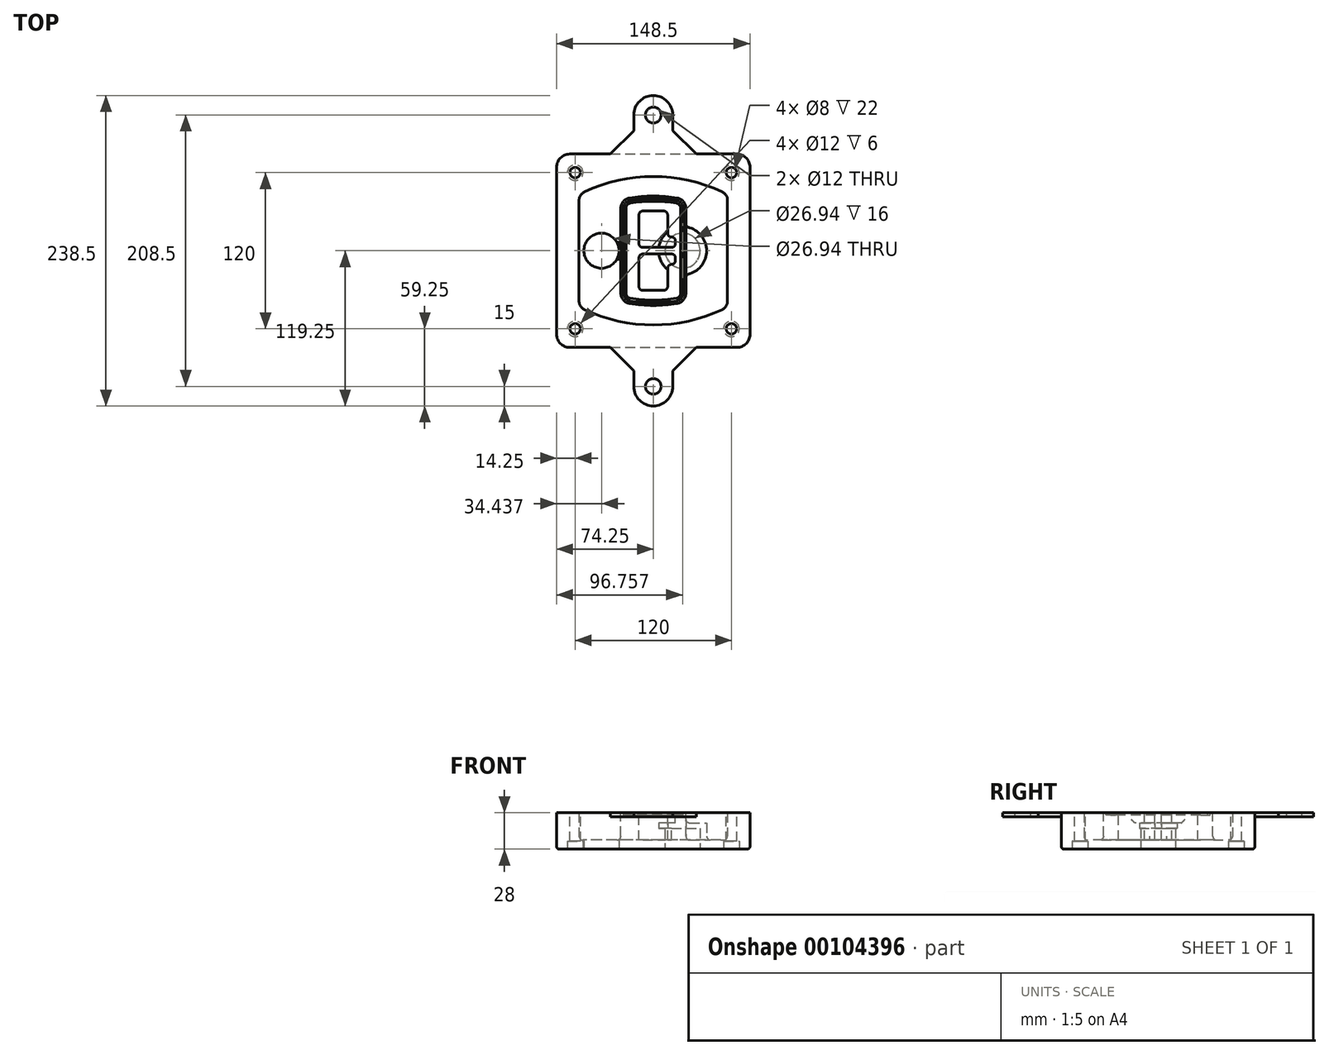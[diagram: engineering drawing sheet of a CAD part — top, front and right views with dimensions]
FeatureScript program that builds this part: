
annotation { "Feature Type Name" : "Feature", "Feature Type Description" : "" }
export const myFeature = defineFeature(function(context is Context, id is Id, definition is map)
    precondition{}
    {
        {
            var Q0;
            Q0=qCreatedBy(makeId("Top.planeOp"),FACE);
            var sketch = newSketch(context, id + "F0", { "sketchPlane" : qUnion([Q0])});
            skPoint(sketch, "E0.rect.middle", {"position": v(0, 0) * mm});
            skLineSegment(sketch, "E1.bottom", {"start": v(-64.25, -74.25) * mm, "end": v(64.25, -74.25) * mm});
            skLineSegment(sketch, "E1.top", {"start": v(-64.25, 74.25) * mm, "end": v(64.25, 74.25) * mm});
            skLineSegment(sketch, "E1.left", {"start": v(-74.25, -64.25) * mm, "end": v(-74.25, 64.25) * mm});
            skLineSegment(sketch, "E1.right", {"start": v(74.25, -64.25) * mm, "end": v(74.25, 64.25) * mm});
            skLineSegment(sketch, "E2", {"start": v(-74.25, 74.25) * mm, "end": v(74.25, -74.25) * mm, "construction": true});
            skLineSegment(sketch, "E3", {"start": v(74.25, 74.25) * mm, "end": v(-74.25, -74.25) * mm, "construction": true});
            skCircle(sketch, "E4", {"center": v(-60, 60) * mm, "radius": 4 * mm});
            skCircle(sketch, "E5", {"center": v(60, 60) * mm, "radius": 4 * mm});
            skCircle(sketch, "E6", {"center": v(60, -60) * mm, "radius": 4 * mm});
            skCircle(sketch, "E7", {"center": v(-60, -60) * mm, "radius": 4 * mm});
            skLineSegment(sketch, "E8", {"start": v(-60, 60) * mm, "end": v(60, 60) * mm, "construction": true});
            skLineSegment(sketch, "E9", {"start": v(60, 60) * mm, "end": v(60, -60) * mm, "construction": true});
            skLineSegment(sketch, "E10", {"start": v(60, -60) * mm, "end": v(-60, -60) * mm, "construction": true});
            skLineSegment(sketch, "E11", {"start": v(-60, -60) * mm, "end": v(-60, 60) * mm, "construction": true});
            skLineSegment(sketch, "E12", {"start": v(-60, 38.83) * mm, "end": v(-60, -38.83) * mm});
            skLineSegment(sketch, "E13", {"start": v(60, 38.83) * mm, "end": v(60, -38.83) * mm});
            skArc(sketch, "E14", {"start": v(54.26, 47.88) * mm, "mid": v(0, 60) * mm, "end": v(-54.26, 47.88) * mm});
            skArc(sketch, "E15", {"start": v(-54.26, -47.88) * mm, "mid": v(0, -60) * mm, "end": v(54.26, -47.88) * mm});
            skLineSegment(sketch, "E16", {"start": v(-60, 0) * mm, "end": v(60, 0) * mm, "construction": true});
            skPoint(sketch, "E17.visualSharp", {"position": v(-60, -45) * mm});
            skArc(sketch, "E17.filletArc", {"start": v(-60, -38.83) * mm, "mid": v(-58.44, -44.2) * mm, "end": v(-54.26, -47.88) * mm});
            skPoint(sketch, "E18.visualSharp", {"position": v(-60, 45) * mm});
            skArc(sketch, "E18.filletArc", {"start": v(-54.26, 47.88) * mm, "mid": v(-58.44, 44.2) * mm, "end": v(-60, 38.83) * mm});
            skPoint(sketch, "E19.visualSharp", {"position": v(60, 45) * mm});
            skArc(sketch, "E19.filletArc", {"start": v(60, 38.83) * mm, "mid": v(58.44, 44.2) * mm, "end": v(54.26, 47.88) * mm});
            skPoint(sketch, "E20.visualSharp", {"position": v(60, -45) * mm});
            skArc(sketch, "E20.filletArc", {"start": v(54.26, -47.88) * mm, "mid": v(58.44, -44.2) * mm, "end": v(60, -38.83) * mm});
            skPoint(sketch, "E21.visualSharp", {"position": v(-74.25, 74.25) * mm});
            skArc(sketch, "E21.filletArc", {"start": v(-64.25, 74.25) * mm, "mid": v(-71.32, 71.32) * mm, "end": v(-74.25, 64.25) * mm});
            skPoint(sketch, "E22.visualSharp", {"position": v(74.25, 74.25) * mm});
            skArc(sketch, "E22.filletArc", {"start": v(74.25, 64.25) * mm, "mid": v(71.32, 71.32) * mm, "end": v(64.25, 74.25) * mm});
            skPoint(sketch, "E23.visualSharp", {"position": v(74.25, -74.25) * mm});
            skArc(sketch, "E23.filletArc", {"start": v(64.25, -74.25) * mm, "mid": v(71.32, -71.32) * mm, "end": v(74.25, -64.25) * mm});
            skPoint(sketch, "E24.visualSharp", {"position": v(-74.25, -74.25) * mm});
            skArc(sketch, "E24.filletArc", {"start": v(-74.25, -64.25) * mm, "mid": v(-71.32, -71.32) * mm, "end": v(-64.25, -74.25) * mm});
            skArc(sketch, "E25.0", {"start": v(57, 38.83) * mm, "mid": v(55.9, 42.58) * mm, "end": v(52.98, 45.17) * mm});
            skLineSegment(sketch, "E25.1", {"start": v(57, 38.83) * mm, "end": v(57, -38.83) * mm});
            skArc(sketch, "E25.2", {"start": v(52.98, -45.17) * mm, "mid": v(55.9, -42.58) * mm, "end": v(57, -38.83) * mm});
            skArc(sketch, "E25.3", {"start": v(-52.98, -45.17) * mm, "mid": v(0, -57) * mm, "end": v(52.98, -45.17) * mm});
            skArc(sketch, "E25.4", {"start": v(-57, -38.83) * mm, "mid": v(-55.9, -42.58) * mm, "end": v(-52.98, -45.17) * mm});
            skArc(sketch, "E25.5", {"start": v(52.98, 45.17) * mm, "mid": v(0, 57) * mm, "end": v(-52.98, 45.17) * mm});
            skLineSegment(sketch, "E25.6", {"start": v(-57, 38.83) * mm, "end": v(-57, -38.83) * mm});
            skArc(sketch, "E25.7", {"start": v(-52.98, 45.17) * mm, "mid": v(-55.9, 42.58) * mm, "end": v(-57, 38.83) * mm});
            skArc(sketch, "E26.0", {"start": v(-55.96, 51.5) * mm, "mid": v(-61.82, 46.33) * mm, "end": v(-64, 38.83) * mm});
            skArc(sketch, "E26.1", {"start": v(55.96, 51.5) * mm, "mid": v(0, 64) * mm, "end": v(-55.96, 51.5) * mm});
            skArc(sketch, "E26.2", {"start": v(64, 38.83) * mm, "mid": v(61.82, 46.33) * mm, "end": v(55.96, 51.5) * mm});
            skLineSegment(sketch, "E26.3", {"start": v(64, 38.83) * mm, "end": v(64, -38.83) * mm});
            skArc(sketch, "E26.4", {"start": v(55.96, -51.5) * mm, "mid": v(61.82, -46.33) * mm, "end": v(64, -38.83) * mm});
            skLineSegment(sketch, "E26.5", {"start": v(-64, 38.83) * mm, "end": v(-64, -38.83) * mm});
            skArc(sketch, "E26.6", {"start": v(-55.96, -51.5) * mm, "mid": v(0, -64) * mm, "end": v(55.96, -51.5) * mm});
            skArc(sketch, "E26.7", {"start": v(-64, -38.83) * mm, "mid": v(-61.82, -46.33) * mm, "end": v(-55.96, -51.5) * mm});
            skSolve(sketch);
        }
        {
            var Q0;
            Q0=makeQuery(id+"F0.imprint","IMPRINT",FACE,{"disambiguationData":[TD([[makeQuery(id+"F0.imprint","IMPRINT",EDGE,{"derivedFrom":sQuery(id+"F0.wireOp",EDGE,"E1.bottom")}),1.0]])]});
            var Q1;
            Q1=makeQuery(id+"F0.imprint","IMPRINT",FACE,{"disambiguationData":[TD([[makeQuery(id+"F0.imprint","IMPRINT",EDGE,{"derivedFrom":sQuery(id+"F0.wireOp",EDGE,"E12")}),1.0]])]});
            var Q2;
            Q2=makeQuery(id+"F0.imprint","IMPRINT",FACE,{"disambiguationData":[TD([[makeQuery(id+"F0.imprint","IMPRINT",EDGE,{"derivedFrom":sQuery(id+"F0.wireOp",EDGE,"E25.0")}),1.0]])]});
            var Q3;
            Q3=makeQuery(id+"F0.imprint","IMPRINT",FACE,{"disambiguationData":[TD([[makeQuery(id+"F0.imprint","IMPRINT",EDGE,{"derivedFrom":sQuery(id+"F0.wireOp",EDGE,"E12")}),-1.0]])]});
            extrude(context, id + "F1", {"entities" : qUnion([Q0, Q1, Q2, Q3]), "oppositeDirection" : true, "depth" : 25 * mm});
        }
        {
            var Q0;
            Q0=makeQuery(id+"F0.imprint","IMPRINT",FACE,{"disambiguationData":[TD([[makeQuery(id+"F0.imprint","IMPRINT",EDGE,{"derivedFrom":sQuery(id+"F0.wireOp",EDGE,"E12")}),1.0]])]});
            extrude(context, id + "F2", {"entities" : qUnion([Q0]), "operationType" : NewBodyOperationType.ADD, "depth" : 3 * mm});
        }
        {
            var Q0;
            Q0=makeQuery(id+"F0.imprint","IMPRINT",FACE,{"disambiguationData":[TD([[makeQuery(id+"F0.imprint","IMPRINT",EDGE,{"derivedFrom":sQuery(id+"F0.wireOp",EDGE,"E25.0")}),1.0]])]});
            extrude(context, id + "F3", {"entities" : qUnion([Q0]), "operationType" : NewBodyOperationType.REMOVE, "oppositeDirection" : true, "depth" : 18 * mm});
        }
        {
            var Q0;
            Q0=makeQuery(id+"F2.opExtrude","CAP_FACE",FACE,{"disambiguationData":[OSD([sQuery(id+"F0.wireOp",EDGE,"E12"),sQuery(id+"F0.wireOp",EDGE,"E13"),sQuery(id+"F0.wireOp",EDGE,"E14"),sQuery(id+"F0.wireOp",EDGE,"E15"),sQuery(id+"F0.wireOp",EDGE,"E17.filletArc"),sQuery(id+"F0.wireOp",EDGE,"E18.filletArc"),sQuery(id+"F0.wireOp",EDGE,"E19.filletArc"),sQuery(id+"F0.wireOp",EDGE,"E20.filletArc"),sQuery(id+"F0.wireOp",EDGE,"E25.0"),sQuery(id+"F0.wireOp",EDGE,"E25.1"),sQuery(id+"F0.wireOp",EDGE,"E25.2"),sQuery(id+"F0.wireOp",EDGE,"E25.3"),sQuery(id+"F0.wireOp",EDGE,"E25.4"),sQuery(id+"F0.wireOp",EDGE,"E25.5"),sQuery(id+"F0.wireOp",EDGE,"E25.6"),sQuery(id+"F0.wireOp",EDGE,"E25.7")])],"isStart":false});
            var sketch = newSketch(context, id + "F4", { "sketchPlane" : qUnion([Q0])});
            skArc(sketch, "E27.0", {"start": v(-18.34, -40.45) * mm, "mid": v(0, -42) * mm, "end": v(18.34, -40.45) * mm});
            skArc(sketch, "E28.0", {"start": v(18.34, 40.45) * mm, "mid": v(0, 42) * mm, "end": v(-18.34, 40.45) * mm});
            skLineSegment(sketch, "E29", {"start": v(-25, 32.57) * mm, "end": v(-25, -32.57) * mm});
            skLineSegment(sketch, "E30", {"start": v(25, 32.57) * mm, "end": v(25, -32.57) * mm});
            skLineSegment(sketch, "E31", {"start": v(-25, 39.1) * mm, "end": v(25, 39.1) * mm, "construction": true});
            skLineSegment(sketch, "E32", {"start": v(-25, -39.1) * mm, "end": v(25, -39.1) * mm, "construction": true});
            skPoint(sketch, "E33.visualSharp", {"position": v(-25, 39.1) * mm});
            skArc(sketch, "E33.filletArc", {"start": v(-18.34, 40.45) * mm, "mid": v(-23.11, 37.73) * mm, "end": v(-25, 32.57) * mm});
            skPoint(sketch, "E34.visualSharp", {"position": v(25, 39.1) * mm});
            skArc(sketch, "E34.filletArc", {"start": v(25, 32.57) * mm, "mid": v(23.11, 37.73) * mm, "end": v(18.34, 40.45) * mm});
            skPoint(sketch, "E35.visualSharp", {"position": v(25, -39.1) * mm});
            skArc(sketch, "E35.filletArc", {"start": v(18.34, -40.45) * mm, "mid": v(23.11, -37.73) * mm, "end": v(25, -32.57) * mm});
            skPoint(sketch, "E36.visualSharp", {"position": v(-25, -39.1) * mm});
            skArc(sketch, "E36.filletArc", {"start": v(-25, -32.57) * mm, "mid": v(-23.11, -37.73) * mm, "end": v(-18.34, -40.45) * mm});
            skArc(sketch, "E37.0", {"start": v(52.98, 45.17) * mm, "mid": v(0, 57) * mm, "end": v(-52.98, 45.17) * mm});
            skArc(sketch, "E37.1", {"start": v(-52.98, 45.17) * mm, "mid": v(-55.9, 42.58) * mm, "end": v(-57, 38.83) * mm});
            skLineSegment(sketch, "E37.2", {"start": v(-57, 38.83) * mm, "end": v(-57, -38.83) * mm});
            skArc(sketch, "E37.3", {"start": v(-57, -38.83) * mm, "mid": v(-55.9, -42.58) * mm, "end": v(-52.98, -45.17) * mm});
            skArc(sketch, "E37.4", {"start": v(-52.98, -45.17) * mm, "mid": v(0, -57) * mm, "end": v(52.98, -45.17) * mm});
            skArc(sketch, "E37.5", {"start": v(52.98, -45.17) * mm, "mid": v(55.9, -42.58) * mm, "end": v(57, -38.83) * mm});
            skLineSegment(sketch, "E37.6", {"start": v(57, 38.83) * mm, "end": v(57, -38.83) * mm});
            skArc(sketch, "E37.7", {"start": v(57, 38.83) * mm, "mid": v(55.9, 42.58) * mm, "end": v(52.98, 45.17) * mm});
            skLineSegment(sketch, "E38.0", {"start": v(23, 32.57) * mm, "end": v(23, -32.57) * mm});
            skArc(sketch, "E38.1", {"start": v(18, -38.48) * mm, "mid": v(21.58, -36.44) * mm, "end": v(23, -32.57) * mm});
            skArc(sketch, "E38.2", {"start": v(-18, -38.48) * mm, "mid": v(0, -40) * mm, "end": v(18, -38.48) * mm});
            skArc(sketch, "E38.3", {"start": v(-23, -32.57) * mm, "mid": v(-21.58, -36.44) * mm, "end": v(-18, -38.48) * mm});
            skLineSegment(sketch, "E38.4", {"start": v(-23, 32.57) * mm, "end": v(-23, -32.57) * mm});
            skArc(sketch, "E38.5", {"start": v(23, 32.57) * mm, "mid": v(21.58, 36.44) * mm, "end": v(18, 38.48) * mm});
            skArc(sketch, "E38.6", {"start": v(-18, 38.48) * mm, "mid": v(-21.58, 36.44) * mm, "end": v(-23, 32.57) * mm});
            skArc(sketch, "E38.7", {"start": v(18, 38.48) * mm, "mid": v(0, 40) * mm, "end": v(-18, 38.48) * mm});
            skArc(sketch, "E39.0", {"start": v(21, 32.57) * mm, "mid": v(20.06, 35.15) * mm, "end": v(17.67, 36.5) * mm});
            skLineSegment(sketch, "E39.1", {"start": v(21, 32.57) * mm, "end": v(21, -32.57) * mm});
            skArc(sketch, "E39.2", {"start": v(17.67, -36.5) * mm, "mid": v(20.06, -35.15) * mm, "end": v(21, -32.57) * mm});
            skArc(sketch, "E39.3", {"start": v(-17.67, -36.5) * mm, "mid": v(0, -38) * mm, "end": v(17.67, -36.5) * mm});
            skArc(sketch, "E39.4", {"start": v(-21, -32.57) * mm, "mid": v(-20.06, -35.15) * mm, "end": v(-17.67, -36.5) * mm});
            skArc(sketch, "E39.5", {"start": v(17.67, 36.5) * mm, "mid": v(0, 38) * mm, "end": v(-17.67, 36.5) * mm});
            skLineSegment(sketch, "E39.6", {"start": v(-21, 32.57) * mm, "end": v(-21, -32.57) * mm});
            skArc(sketch, "E39.7", {"start": v(-17.67, 36.5) * mm, "mid": v(-20.06, 35.15) * mm, "end": v(-21, 32.57) * mm});
            skLineSegment(sketch, "E40", {"start": v(-25, 0) * mm, "end": v(25, 0) * mm, "construction": true});
            skLineSegment(sketch, "E41", {"start": v(-11, 5.5) * mm, "end": v(-11, 27.5) * mm});
            skLineSegment(sketch, "E42", {"start": v(-8, 30.5) * mm, "end": v(8, 30.5) * mm});
            skLineSegment(sketch, "E43", {"start": v(11, 27.5) * mm, "end": v(11, 13.5) * mm});
            skLineSegment(sketch, "E44", {"start": v(14, 10.5) * mm, "end": v(14, 10.5) * mm});
            skLineSegment(sketch, "E45", {"start": v(17, 7.5) * mm, "end": v(17, 5.5) * mm});
            skLineSegment(sketch, "E46", {"start": v(14, 2.5) * mm, "end": v(-8, 2.5) * mm});
            skPoint(sketch, "E47.visualSharp", {"position": v(-11, 30.5) * mm});
            skArc(sketch, "E47.filletArc", {"start": v(-8, 30.5) * mm, "mid": v(-10.12, 29.62) * mm, "end": v(-11, 27.5) * mm});
            skPoint(sketch, "E48.visualSharp", {"position": v(11, 30.5) * mm});
            skArc(sketch, "E48.filletArc", {"start": v(11, 27.5) * mm, "mid": v(10.12, 29.62) * mm, "end": v(8, 30.5) * mm});
            skPoint(sketch, "E49.visualSharp", {"position": v(11, 10.5) * mm});
            skArc(sketch, "E49.filletArc", {"start": v(11, 13.5) * mm, "mid": v(11.88, 11.38) * mm, "end": v(14, 10.5) * mm});
            skPoint(sketch, "E50.visualSharp", {"position": v(17, 10.5) * mm});
            skArc(sketch, "E50.filletArc", {"start": v(17, 7.5) * mm, "mid": v(16.12, 9.62) * mm, "end": v(14, 10.5) * mm});
            skPoint(sketch, "E51.visualSharp", {"position": v(17, 2.5) * mm});
            skArc(sketch, "E51.filletArc", {"start": v(14, 2.5) * mm, "mid": v(16.12, 3.38) * mm, "end": v(17, 5.5) * mm});
            skPoint(sketch, "E52.visualSharp", {"position": v(-11, 2.5) * mm});
            skArc(sketch, "E52.filletArc", {"start": v(-11, 5.5) * mm, "mid": v(-10.12, 3.38) * mm, "end": v(-8, 2.5) * mm});
            skLineSegment(sketch, "E53.0.MirrorCS", {"start": v(14, -2.5) * mm, "end": v(-8, -2.5) * mm});
            skArc(sketch, "E54.0.MirrorCS", {"start": v(-11, -5.5) * mm, "mid": v(-10.12, -3.38) * mm, "end": v(-8, -2.5) * mm});
            skLineSegment(sketch, "E55.0.MirrorCS", {"start": v(-11, -5.5) * mm, "end": v(-11, -27.5) * mm});
            skArc(sketch, "E56.0.MirrorCS", {"start": v(-8, -30.5) * mm, "mid": v(-10.12, -29.62) * mm, "end": v(-11, -27.5) * mm});
            skLineSegment(sketch, "E57.0.MirrorCS", {"start": v(-8, -30.5) * mm, "end": v(8, -30.5) * mm});
            skArc(sketch, "E58.0.MirrorCS", {"start": v(11, -27.5) * mm, "mid": v(10.12, -29.62) * mm, "end": v(8, -30.5) * mm});
            skLineSegment(sketch, "E59.0.MirrorCS", {"start": v(11, -27.5) * mm, "end": v(11, -13.5) * mm});
            skArc(sketch, "E60.0.MirrorCS", {"start": v(11, -13.5) * mm, "mid": v(11.88, -11.38) * mm, "end": v(14, -10.5) * mm});
            skArc(sketch, "E61.0.MirrorCS", {"start": v(17, -7.5) * mm, "mid": v(16.12, -9.62) * mm, "end": v(14, -10.5) * mm});
            skLineSegment(sketch, "E62.0.MirrorCS", {"start": v(17, -7.5) * mm, "end": v(17, -5.5) * mm});
            skArc(sketch, "E63.0.MirrorCS", {"start": v(14, -2.5) * mm, "mid": v(16.12, -3.38) * mm, "end": v(17, -5.5) * mm});
            skSolve(sketch);
        }
        {
            var Q0;
            Q0=makeQuery(id+"F4.imprint","IMPRINT",FACE,{"disambiguationData":[TD([[makeQuery(id+"F4.imprint","IMPRINT",EDGE,{"derivedFrom":sQuery(id+"F4.wireOp",EDGE,"E27.0")}),1.0]])]});
            var Q1;
            Q1=makeQuery(id+"F4.imprint","IMPRINT",FACE,{"disambiguationData":[TD([[makeQuery(id+"F4.imprint","IMPRINT",EDGE,{"derivedFrom":sQuery(id+"F4.wireOp",EDGE,"E38.0")}),-1.0]])]});
            var Q2;
            Q2=makeQuery(id+"F4.imprint","IMPRINT",FACE,{"disambiguationData":[TD([[makeQuery(id+"F4.imprint","IMPRINT",EDGE,{"derivedFrom":sQuery(id+"F4.wireOp",EDGE,"E39.0")}),1.0]])]});
            extrude(context, id + "F5", {"entities" : qUnion([Q0, Q1, Q2]), "operationType" : NewBodyOperationType.ADD, "endBound" : BoundingType.UP_TO_NEXT, "oppositeDirection" : true, "depth" : 25 * mm});
        }
        {
            var Q0;
            Q0=makeQuery(id+"F4.imprint","IMPRINT",FACE,{"disambiguationData":[TD([[makeQuery(id+"F4.imprint","IMPRINT",EDGE,{"derivedFrom":sQuery(id+"F4.wireOp",EDGE,"E38.0")}),-1.0]])]});
            extrude(context, id + "F6", {"entities" : qUnion([Q0]), "operationType" : NewBodyOperationType.REMOVE, "oppositeDirection" : true, "depth" : 2 * mm});
        }
        {
            var Q0;
            Q0=makeQuery(id+"F1.opExtrude","CAP_FACE",FACE,{"disambiguationData":[OSD([sQuery(id+"F0.wireOp",EDGE,"E1.bottom"),sQuery(id+"F0.wireOp",EDGE,"E1.top"),sQuery(id+"F0.wireOp",EDGE,"E1.left"),sQuery(id+"F0.wireOp",EDGE,"E1.right"),sQuery(id+"F0.wireOp",EDGE,"E4"),sQuery(id+"F0.wireOp",EDGE,"E5"),sQuery(id+"F0.wireOp",EDGE,"E6"),sQuery(id+"F0.wireOp",EDGE,"E7"),sQuery(id+"F0.wireOp",EDGE,"E21.filletArc"),sQuery(id+"F0.wireOp",EDGE,"E22.filletArc"),sQuery(id+"F0.wireOp",EDGE,"E23.filletArc"),sQuery(id+"F0.wireOp",EDGE,"E24.filletArc")])],"isStart":false});
            var sketch = newSketch(context, id + "F7", { "sketchPlane" : qUnion([Q0])});
            skCircle(sketch, "E64", {"center": v(22.5, 0) * mm, "radius": 13.47 * mm});
            skCircle(sketch, "E65", {"center": v(-39.81, 0) * mm, "radius": 13.47 * mm});
            skLineSegment(sketch, "E66", {"start": v(74.25, 0) * mm, "end": v(-74.25, 0) * mm});
            skCircle(sketch, "E67", {"center": v(22.5, 0) * mm, "radius": 18.47 * mm});
            skCircle(sketch, "E68", {"center": v(60, -60) * mm, "radius": 6 * mm});
            skCircle(sketch, "E69", {"center": v(-60, -60) * mm, "radius": 6 * mm});
            skCircle(sketch, "E70", {"center": v(-60, 60) * mm, "radius": 6 * mm});
            skCircle(sketch, "E71", {"center": v(60, 60) * mm, "radius": 6 * mm});
            skSolve(sketch);
        }
        {
            var Q0;
            {var subQ1=sQuery(id+"F7.wireOp",EDGE,"E66");var subQ4=sQuery(id+"F7.wireOp",EDGE,"E64");var subQ6=makeQuery(id+"F7.imprint","INTERSECT",VERTEX,{"disambiguationData":[OD(0.0)],"derivedFrom":[subQ4,subQ1]});Q0=makeQuery(id+"F7.imprint","IMPRINT",FACE,{"disambiguationData":[TD([[makeQuery(id+"F7.imprint","IMPRINT",EDGE,{"disambiguationData":[TD([[subQ6,-1.0]])],"derivedFrom":subQ4}),-1.0]])]});}
            var Q1;
            {var subQ0=sQuery(id+"F7.wireOp",EDGE,"E66");var subQ1=sQuery(id+"F7.wireOp",EDGE,"E64");var subQ3=makeQuery(id+"F7.imprint","INTERSECT",VERTEX,{"disambiguationData":[OD(0.0)],"derivedFrom":[subQ1,subQ0]});Q1=makeQuery(id+"F7.imprint","IMPRINT",FACE,{"disambiguationData":[TD([[makeQuery(id+"F7.imprint","IMPRINT",EDGE,{"disambiguationData":[TD([[subQ3,-1.0]])],"derivedFrom":subQ1}),1.0]])]});}
            var Q2;
            {var subQ0=sQuery(id+"F7.wireOp",EDGE,"E66");var subQ1=sQuery(id+"F7.wireOp",EDGE,"E64");var subQ3=makeQuery(id+"F7.imprint","INTERSECT",VERTEX,{"disambiguationData":[OD(0.0)],"derivedFrom":[subQ1,subQ0]});Q2=makeQuery(id+"F7.imprint","IMPRINT",FACE,{"disambiguationData":[TD([[makeQuery(id+"F7.imprint","IMPRINT",EDGE,{"disambiguationData":[TD([[subQ3,1.0]])],"derivedFrom":subQ1}),1.0]])]});}
            var Q3;
            {var subQ1=sQuery(id+"F7.wireOp",EDGE,"E66");var subQ4=sQuery(id+"F7.wireOp",EDGE,"E64");var subQ6=makeQuery(id+"F7.imprint","INTERSECT",VERTEX,{"disambiguationData":[OD(0.0)],"derivedFrom":[subQ4,subQ1]});Q3=makeQuery(id+"F7.imprint","IMPRINT",FACE,{"disambiguationData":[TD([[makeQuery(id+"F7.imprint","IMPRINT",EDGE,{"disambiguationData":[TD([[subQ6,1.0]])],"derivedFrom":subQ4}),-1.0]])]});}
            extrude(context, id + "F8", {"entities" : qUnion([Q0, Q1, Q2, Q3]), "operationType" : NewBodyOperationType.ADD, "oppositeDirection" : true, "depth" : 20 * mm});
        }
        {
            var Q0;
            {var subQ0=sQuery(id+"F7.wireOp",EDGE,"E66");var subQ1=sQuery(id+"F7.wireOp",EDGE,"E64");var subQ3=makeQuery(id+"F7.imprint","INTERSECT",VERTEX,{"disambiguationData":[OD(0.0)],"derivedFrom":[subQ1,subQ0]});Q0=makeQuery(id+"F7.imprint","IMPRINT",FACE,{"disambiguationData":[TD([[makeQuery(id+"F7.imprint","IMPRINT",EDGE,{"disambiguationData":[TD([[subQ3,-1.0]])],"derivedFrom":subQ1}),1.0]])]});}
            var Q1;
            {var subQ0=sQuery(id+"F7.wireOp",EDGE,"E66");var subQ1=sQuery(id+"F7.wireOp",EDGE,"E64");var subQ3=makeQuery(id+"F7.imprint","INTERSECT",VERTEX,{"disambiguationData":[OD(0.0)],"derivedFrom":[subQ1,subQ0]});Q1=makeQuery(id+"F7.imprint","IMPRINT",FACE,{"disambiguationData":[TD([[makeQuery(id+"F7.imprint","IMPRINT",EDGE,{"disambiguationData":[TD([[subQ3,1.0]])],"derivedFrom":subQ1}),1.0]])]});}
            extrude(context, id + "F9", {"entities" : qUnion([Q0, Q1]), "operationType" : NewBodyOperationType.REMOVE, "oppositeDirection" : true, "depth" : 16 * mm});
        }
        {
            var Q0;
            {var subQ0=sQuery(id+"F7.wireOp",EDGE,"E66");var subQ1=sQuery(id+"F7.wireOp",EDGE,"E65");var subQ3=makeQuery(id+"F7.imprint","INTERSECT",VERTEX,{"disambiguationData":[OD(0.0)],"derivedFrom":[subQ1,subQ0]});Q0=makeQuery(id+"F7.imprint","IMPRINT",FACE,{"disambiguationData":[TD([[makeQuery(id+"F7.imprint","IMPRINT",EDGE,{"disambiguationData":[TD([[subQ3,-1.0]])],"derivedFrom":subQ1}),1.0]])]});}
            var Q1;
            {var subQ0=sQuery(id+"F7.wireOp",EDGE,"E66");var subQ1=sQuery(id+"F7.wireOp",EDGE,"E65");var subQ3=makeQuery(id+"F7.imprint","INTERSECT",VERTEX,{"disambiguationData":[OD(0.0)],"derivedFrom":[subQ1,subQ0]});Q1=makeQuery(id+"F7.imprint","IMPRINT",FACE,{"disambiguationData":[TD([[makeQuery(id+"F7.imprint","IMPRINT",EDGE,{"disambiguationData":[TD([[subQ3,1.0]])],"derivedFrom":subQ1}),1.0]])]});}
            extrude(context, id + "F10", {"entities" : qUnion([Q0, Q1]), "operationType" : NewBodyOperationType.REMOVE, "oppositeDirection" : true, "depth" : 25 * mm});
        }
        {
            var Q0;
            Q0=makeQuery(id+"F7.imprint","IMPRINT",FACE,{"disambiguationData":[TD([[makeQuery(id+"F7.imprint","IMPRINT",EDGE,{"derivedFrom":sQuery(id+"F7.wireOp",EDGE,"E68")}),1.0]])]});
            var Q1;
            Q1=makeQuery(id+"F7.imprint","IMPRINT",FACE,{"disambiguationData":[TD([[makeQuery(id+"F7.imprint","IMPRINT",EDGE,{"derivedFrom":makeQuery(id+"F1.opExtrude","CAP_EDGE",EDGE,{"disambiguationData":[OSD([sQuery(id+"F0.wireOp",EDGE,"E5")])],"isStart":false})}),-1.0]])]});
            var Q2;
            Q2=makeQuery(id+"F7.imprint","IMPRINT",FACE,{"disambiguationData":[TD([[makeQuery(id+"F7.imprint","IMPRINT",EDGE,{"derivedFrom":sQuery(id+"F7.wireOp",EDGE,"E69")}),1.0]])]});
            var Q3;
            Q3=makeQuery(id+"F7.imprint","IMPRINT",FACE,{"disambiguationData":[TD([[makeQuery(id+"F7.imprint","IMPRINT",EDGE,{"derivedFrom":makeQuery(id+"F1.opExtrude","CAP_EDGE",EDGE,{"disambiguationData":[OSD([sQuery(id+"F0.wireOp",EDGE,"E4")])],"isStart":false})}),-1.0]])]});
            var Q4;
            Q4=makeQuery(id+"F7.imprint","IMPRINT",FACE,{"disambiguationData":[TD([[makeQuery(id+"F7.imprint","IMPRINT",EDGE,{"derivedFrom":sQuery(id+"F7.wireOp",EDGE,"E70")}),1.0]])]});
            var Q5;
            Q5=makeQuery(id+"F7.imprint","IMPRINT",FACE,{"disambiguationData":[TD([[makeQuery(id+"F7.imprint","IMPRINT",EDGE,{"derivedFrom":makeQuery(id+"F1.opExtrude","CAP_EDGE",EDGE,{"disambiguationData":[OSD([sQuery(id+"F0.wireOp",EDGE,"E7")])],"isStart":false})}),-1.0]])]});
            var Q6;
            Q6=makeQuery(id+"F7.imprint","IMPRINT",FACE,{"disambiguationData":[TD([[makeQuery(id+"F7.imprint","IMPRINT",EDGE,{"derivedFrom":sQuery(id+"F7.wireOp",EDGE,"E71")}),1.0]])]});
            var Q7;
            Q7=makeQuery(id+"F7.imprint","IMPRINT",FACE,{"disambiguationData":[TD([[makeQuery(id+"F7.imprint","IMPRINT",EDGE,{"derivedFrom":makeQuery(id+"F1.opExtrude","CAP_EDGE",EDGE,{"disambiguationData":[OSD([sQuery(id+"F0.wireOp",EDGE,"E6")])],"isStart":false})}),-1.0]])]});
            extrude(context, id + "F11", {"entities" : qUnion([Q0, Q1, Q2, Q3, Q4, Q5, Q6, Q7]), "operationType" : NewBodyOperationType.REMOVE, "oppositeDirection" : true, "depth" : 6 * mm});
        }
        {
            var Q0;
            Q0=makeQuery(id+"F9.boolean.opBoolean","COPY",FACE,{"derivedFrom":makeQuery(id+"F9.opExtrude","CAP_FACE",FACE,{"disambiguationData":[OSD([sQuery(id+"F7.wireOp",EDGE,"E64")])],"isStart":false})});
            var sketch = newSketch(context, id + "F12", { "sketchPlane" : qUnion([Q0])});
            skArc(sketch, "E72.0", {"start": v(11, 14.45) * mm, "mid": v(6.45, 9.13) * mm, "end": v(4.2, 2.5) * mm});
            skArc(sketch, "E72.1", {"start": v(4.2, -2.5) * mm, "mid": v(6.45, -9.13) * mm, "end": v(11, -14.45) * mm});
            skLineSegment(sketch, "E73", {"start": v(4.2, -2.5) * mm, "end": v(14, -2.5) * mm});
            skLineSegment(sketch, "E74.0", {"start": v(14, 2.5) * mm, "end": v(4.2, 2.5) * mm});
            skArc(sketch, "E74.1", {"start": v(14, 2.5) * mm, "mid": v(16.12, 3.38) * mm, "end": v(17, 5.5) * mm});
            skLineSegment(sketch, "E74.2", {"start": v(17, 7.5) * mm, "end": v(17, 5.5) * mm});
            skArc(sketch, "E74.3", {"start": v(17, 7.5) * mm, "mid": v(16.12, 9.62) * mm, "end": v(14, 10.5) * mm});
            skArc(sketch, "E74.4", {"start": v(11, 13.5) * mm, "mid": v(11.88, 11.38) * mm, "end": v(14, 10.5) * mm});
            skLineSegment(sketch, "E74.5", {"start": v(11, 14.45) * mm, "end": v(11, 13.5) * mm});
            skLineSegment(sketch, "E74.7", {"start": v(14, -2.5) * mm, "end": v(4.2, -2.5) * mm});
            skArc(sketch, "E74.8", {"start": v(14, -2.5) * mm, "mid": v(16.12, -3.38) * mm, "end": v(17, -5.5) * mm});
            skLineSegment(sketch, "E74.9", {"start": v(17, -7.5) * mm, "end": v(17, -5.5) * mm});
            skArc(sketch, "E74.10", {"start": v(17, -7.5) * mm, "mid": v(16.12, -9.62) * mm, "end": v(14, -10.5) * mm});
            skArc(sketch, "E74.11", {"start": v(11, -13.5) * mm, "mid": v(11.88, -11.38) * mm, "end": v(14, -10.5) * mm});
            skLineSegment(sketch, "E74.12", {"start": v(11, -14.45) * mm, "end": v(11, -13.5) * mm});
            skPoint(sketch, "E75.orphan", {"position": v(11, -27.5) * mm});
            skPoint(sketch, "E76.orphan", {"position": v(-8, -2.5) * mm});
            skPoint(sketch, "E77.orphan", {"position": v(-8, 2.5) * mm});
            skPoint(sketch, "E78.orphan", {"position": v(11, 27.5) * mm});
            skSolve(sketch);
        }
        {
            var Q0;
            {var subQ7=sQuery(id+"F12.wireOp",EDGE,"E72.0");var subQ14=sQuery(id+"F12.wireOp",EDGE,"E72.1");var subQ16=sQuery(id+"F12.wireOp",EDGE,"E74.1");var subQ18=sQuery(id+"F12.wireOp",EDGE,"E74.8");Q0=qUnion([makeQuery(id+"F12.imprint","IMPRINT",FACE,{"disambiguationData":[TD([[makeQuery(id+"F12.imprint","IMPRINT",EDGE,{"derivedFrom":subQ7}),1.0]])]}),makeQuery(id+"F12.imprint","IMPRINT",FACE,{"disambiguationData":[TD([[makeQuery(id+"F12.imprint","IMPRINT",EDGE,{"derivedFrom":subQ14}),1.0]])]}),makeQuery(id+"F12.imprint","IMPRINT",FACE,{"disambiguationData":[TD([[makeQuery(id+"F12.imprint","IMPRINT",EDGE,{"derivedFrom":subQ16}),1.0]])]}),makeQuery(id+"F12.imprint","IMPRINT",FACE,{"disambiguationData":[TD([[makeQuery(id+"F12.imprint","IMPRINT",EDGE,{"derivedFrom":subQ18}),-1.0]])]})]);}
            var Q1;
            Q1=makeQuery(id+"F5.boolean.opBoolean","SPLIT",FACE,{"disambiguationData":[TD([makeQuery(id+"F5.opExtrude","SWEPT_FACE",FACE,{"disambiguationData":[OSD([sQuery(id+"F4.wireOp",EDGE,"E41")])]})])],"derivedFrom":makeQuery(id+"F3.boolean.opBoolean","COPY",FACE,{"derivedFrom":makeQuery(id+"F3.opExtrude","CAP_FACE",FACE,{"disambiguationData":[OSD([sQuery(id+"F0.wireOp",EDGE,"E25.0"),sQuery(id+"F0.wireOp",EDGE,"E25.1"),sQuery(id+"F0.wireOp",EDGE,"E25.2"),sQuery(id+"F0.wireOp",EDGE,"E25.3"),sQuery(id+"F0.wireOp",EDGE,"E25.4"),sQuery(id+"F0.wireOp",EDGE,"E25.5"),sQuery(id+"F0.wireOp",EDGE,"E25.6"),sQuery(id+"F0.wireOp",EDGE,"E25.7")])],"isStart":false})})});
            extrude(context, id + "F13", {"entities" : qUnion([Q0]), "operationType" : NewBodyOperationType.REMOVE, "endBound" : BoundingType.UP_TO_SURFACE, "endBoundEntityFace" : qUnion([Q1]), "depth" : 25 * mm});
        }
        {
            var Q0;
            Q0=makeQuery(id+"F3.boolean.opBoolean","COPY",EDGE,{"derivedFrom":makeQuery(id+"F3.opExtrude","CAP_EDGE",EDGE,{"disambiguationData":[OSD([sQuery(id+"F0.wireOp",EDGE,"E25.6")])],"isStart":false})});
            var Q1;
            Q1=makeQuery(id+"F8.boolean.opBoolean","INTERSECT",EDGE,{"derivedFrom":[makeQuery(id+"F5.opExtrude","SWEPT_FACE",FACE,{"disambiguationData":[OSD([sQuery(id+"F4.wireOp",EDGE,"E30")])]}),makeQuery(id+"F8.opExtrude","CAP_FACE",FACE,{"disambiguationData":[OSD([sQuery(id+"F7.wireOp",EDGE,"E67")])],"isStart":false})]});
            var Q2;
            Q2=makeQuery(id+"F8.boolean.opBoolean","INTERSECT",EDGE,{"disambiguationData":[OD(1.0)],"derivedFrom":[makeQuery(id+"F5.opExtrude","SWEPT_FACE",FACE,{"disambiguationData":[OSD([sQuery(id+"F4.wireOp",EDGE,"E30")])]}),makeQuery(id+"F8.opExtrude","SWEPT_FACE",FACE,{"disambiguationData":[OSD([sQuery(id+"F7.wireOp",EDGE,"E67")])]})]});
            var Q3;
            {var subQ0=sQuery(id+"F4.wireOp",EDGE,"E30");Q3=makeQuery(id+"F8.boolean.opBoolean","SPLIT",EDGE,{"disambiguationData":[TD([makeQuery(id+"F5.opExtrude","SWEPT_FACE",FACE,{"disambiguationData":[OSD([sQuery(id+"F4.wireOp",EDGE,"E35.filletArc")])]})])],"derivedFrom":makeQuery(id+"F5.opExtrude","CAP_EDGE",EDGE,{"disambiguationData":[OSD([subQ0])],"isStart":false})});}
            var Q4;
            {var subQ0=sQuery(id+"F0.wireOp",EDGE,"E25.7");var subQ1=sQuery(id+"F0.wireOp",EDGE,"E25.1");var subQ2=sQuery(id+"F0.wireOp",EDGE,"E25.6");var subQ3=sQuery(id+"F0.wireOp",EDGE,"E25.5");var subQ4=sQuery(id+"F0.wireOp",EDGE,"E25.4");var subQ5=sQuery(id+"F0.wireOp",EDGE,"E25.0");var subQ6=sQuery(id+"F0.wireOp",EDGE,"E25.2");var subQ7=sQuery(id+"F0.wireOp",EDGE,"E25.3");Q4=makeQuery(id+"F8.boolean.opBoolean","INTERSECT",EDGE,{"derivedFrom":[makeQuery(id+"F5.boolean.opBoolean","SPLIT",FACE,{"disambiguationData":[TD([makeQuery(id+"F2.opExtrude","SWEPT_FACE",FACE,{"disambiguationData":[OSD([subQ5])]})])],"derivedFrom":makeQuery(id+"F3.boolean.opBoolean","COPY",FACE,{"derivedFrom":makeQuery(id+"F3.opExtrude","CAP_FACE",FACE,{"disambiguationData":[OSD([subQ5,subQ1,subQ6,subQ7,subQ4,subQ3,subQ2,subQ0])],"isStart":false})})}),makeQuery(id+"F8.opExtrude","SWEPT_FACE",FACE,{"disambiguationData":[OSD([sQuery(id+"F7.wireOp",EDGE,"E67")])]})]});}
            var Q5;
            Q5=makeQuery(id+"F8.boolean.opBoolean","INTERSECT",EDGE,{"disambiguationData":[OD(0.0)],"derivedFrom":[makeQuery(id+"F5.opExtrude","SWEPT_FACE",FACE,{"disambiguationData":[OSD([sQuery(id+"F4.wireOp",EDGE,"E30")])]}),makeQuery(id+"F8.opExtrude","SWEPT_FACE",FACE,{"disambiguationData":[OSD([sQuery(id+"F7.wireOp",EDGE,"E67")])]})]});
            fillet(context, id + "F14", {"entities" : qUnion([Q0, Q1, Q2, Q3, Q4, Q5]), "radius" : 3 * mm, "tangentPropagation" : true, "allowEdgeOverflow" : false});
        }
        {
            var Q0;
            Q0=makeQuery(id+"F1.opExtrude","CAP_EDGE",EDGE,{"disambiguationData":[OSD([sQuery(id+"F0.wireOp",EDGE,"E1.bottom")])],"isStart":false});
            fillet(context, id + "F15", {"entities" : qUnion([Q0]), "radius" : 2 * mm, "tangentPropagation" : true, "allowEdgeOverflow" : false});
        }
        {
            var Q0;
            {var subQ0=sQuery(id+"F0.wireOp",EDGE,"E22.filletArc");var subQ1=sQuery(id+"F0.wireOp",EDGE,"E7");var subQ2=sQuery(id+"F0.wireOp",EDGE,"E6");var subQ3=sQuery(id+"F0.wireOp",EDGE,"E5");var subQ4=sQuery(id+"F0.wireOp",EDGE,"E4");var subQ5=sQuery(id+"F0.wireOp",EDGE,"E1.bottom");var subQ6=sQuery(id+"F0.wireOp",EDGE,"E21.filletArc");var subQ7=sQuery(id+"F0.wireOp",EDGE,"E1.top");var subQ8=sQuery(id+"F0.wireOp",EDGE,"E1.left");var subQ9=sQuery(id+"F0.wireOp",EDGE,"E1.right");var subQ10=sQuery(id+"F0.wireOp",EDGE,"E23.filletArc");var subQ11=sQuery(id+"F0.wireOp",EDGE,"E24.filletArc");Q0=makeQuery(id+"F2.boolean.opBoolean","SPLIT",FACE,{"disambiguationData":[TD([makeQuery(id+"F1.opExtrude","SWEPT_FACE",FACE,{"disambiguationData":[OSD([subQ5])]})])],"derivedFrom":makeQuery(id+"F1.opExtrude","CAP_FACE",FACE,{"disambiguationData":[OSD([subQ5,subQ7,subQ8,subQ9,subQ4,subQ3,subQ2,subQ1,subQ6,subQ0,subQ10,subQ11])],"isStart":true})});}
            var sketch = newSketch(context, id + "F16", { "sketchPlane" : qUnion([Q0])});
            skLineSegment(sketch, "E79", {"start": v(0, 74.25) * mm, "end": v(0, 104.25) * mm});
            skCircle(sketch, "E80", {"center": v(0, 104.25) * mm, "radius": 6 * mm});
            skLineSegment(sketch, "E81", {"start": v(-33, 74.25) * mm, "end": v(-15, 92.25) * mm});
            skLineSegment(sketch, "E82", {"start": v(-15, 92.25) * mm, "end": v(-15, 104.25) * mm});
            skArc(sketch, "E83", {"start": v(15, 104.25) * mm, "mid": v(0, 119.25) * mm, "end": v(-15, 104.25) * mm});
            skLineSegment(sketch, "E84", {"start": v(15, 104.25) * mm, "end": v(15, 92.25) * mm});
            skLineSegment(sketch, "E85", {"start": v(15, 92.25) * mm, "end": v(33, 74.25) * mm});
            skLineSegment(sketch, "E86", {"start": v(-74.25, 0) * mm, "end": v(74.25, 0) * mm, "construction": true});
            skLineSegment(sketch, "E87.MirrorCS", {"start": v(-33, -74.25) * mm, "end": v(-15, -92.25) * mm});
            skLineSegment(sketch, "E88.MirrorCS", {"start": v(15, -92.25) * mm, "end": v(33, -74.25) * mm});
            skCircle(sketch, "E89.MirrorC", {"center": v(0, -104.25) * mm, "radius": 6 * mm});
            skLineSegment(sketch, "E90.MirrorCS", {"start": v(0, -74.25) * mm, "end": v(0, -104.25) * mm});
            skArc(sketch, "E91.MirrorCS", {"start": v(15, -104.25) * mm, "mid": v(0, -119.25) * mm, "end": v(-15, -104.25) * mm});
            skLineSegment(sketch, "E92.MirrorCS", {"start": v(-15, -92.25) * mm, "end": v(-15, -104.25) * mm});
            skLineSegment(sketch, "E93.MirrorCS", {"start": v(15, -104.25) * mm, "end": v(15, -92.25) * mm});
            skSolve(sketch);
        }
        {
            var Q0;
            Q0=makeQuery(id+"F16.imprint","IMPRINT",FACE,{"disambiguationData":[TD([[makeQuery(id+"F16.imprint","IMPRINT",EDGE,{"derivedFrom":makeQuery(id+"F1.opExtrude","CAP_EDGE",EDGE,{"disambiguationData":[OSD([sQuery(id+"F0.wireOp",EDGE,"E1.left")])],"isStart":true})}),-1.0]])]});
            var Q1;
            {var subQ3=sQuery(id+"F16.wireOp",EDGE,"E87.MirrorCS");Q1=makeQuery(id+"F16.imprint","IMPRINT",FACE,{"disambiguationData":[TD([[makeQuery(id+"F16.imprint","IMPRINT",EDGE,{"derivedFrom":subQ3}),1.0]])]});}
            var Q2;
            Q2=makeQuery(id+"F16.imprint","IMPRINT",FACE,{"disambiguationData":[TD([[makeQuery(id+"F16.imprint","IMPRINT",EDGE,{"derivedFrom":sQuery(id+"F16.wireOp",EDGE,"E80")}),-1.0]])]});
            var Q3;
            Q3=makeQuery(id+"F2.opExtrude","CAP_FACE",FACE,{"disambiguationData":[OSD([sQuery(id+"F0.wireOp",EDGE,"E12"),sQuery(id+"F0.wireOp",EDGE,"E13"),sQuery(id+"F0.wireOp",EDGE,"E14"),sQuery(id+"F0.wireOp",EDGE,"E15"),sQuery(id+"F0.wireOp",EDGE,"E17.filletArc"),sQuery(id+"F0.wireOp",EDGE,"E18.filletArc"),sQuery(id+"F0.wireOp",EDGE,"E19.filletArc"),sQuery(id+"F0.wireOp",EDGE,"E20.filletArc"),sQuery(id+"F0.wireOp",EDGE,"E25.0"),sQuery(id+"F0.wireOp",EDGE,"E25.1"),sQuery(id+"F0.wireOp",EDGE,"E25.2"),sQuery(id+"F0.wireOp",EDGE,"E25.3"),sQuery(id+"F0.wireOp",EDGE,"E25.4"),sQuery(id+"F0.wireOp",EDGE,"E25.5"),sQuery(id+"F0.wireOp",EDGE,"E25.6"),sQuery(id+"F0.wireOp",EDGE,"E25.7")])],"isStart":false});
            extrude(context, id + "F17", {"entities" : qUnion([Q0, Q1, Q2]), "operationType" : NewBodyOperationType.ADD, "endBound" : BoundingType.UP_TO_SURFACE, "endBoundEntityFace" : qUnion([Q3]), "depth" : 25 * mm});
        }
    });
